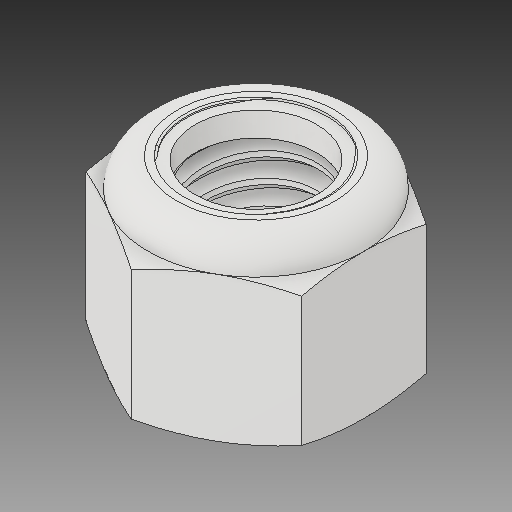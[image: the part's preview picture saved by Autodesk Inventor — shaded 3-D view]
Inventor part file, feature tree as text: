
AUTODESK INVENTOR PART (.ipt)
format: ipt  version: 2018 (Build 220112000, 112)  size: 336,896 bytes
history: native  units: in
note: dims shown in document units (in); Inventor stores cm internally (conversion verified against a paired STEP export)
features: other x1, revolve x1
ambient origin geometry x8: Origin, YZ Plane, XZ Plane, XY Plane, X Axis, Y Axis, Z Axis, Center Point
bodies: Solid1 (feature_tree), Solid2 (feature_tree)
feature tree (2):
  other  "Cut-Revolve4"
  revolve  "Revolve2"  [1 undecoded]
note: 1 required parameter value undecoded (feature->parameter linkage not recoverable at this tier; creation-order binding heuristic only, values carry confidence <= 0.55)
